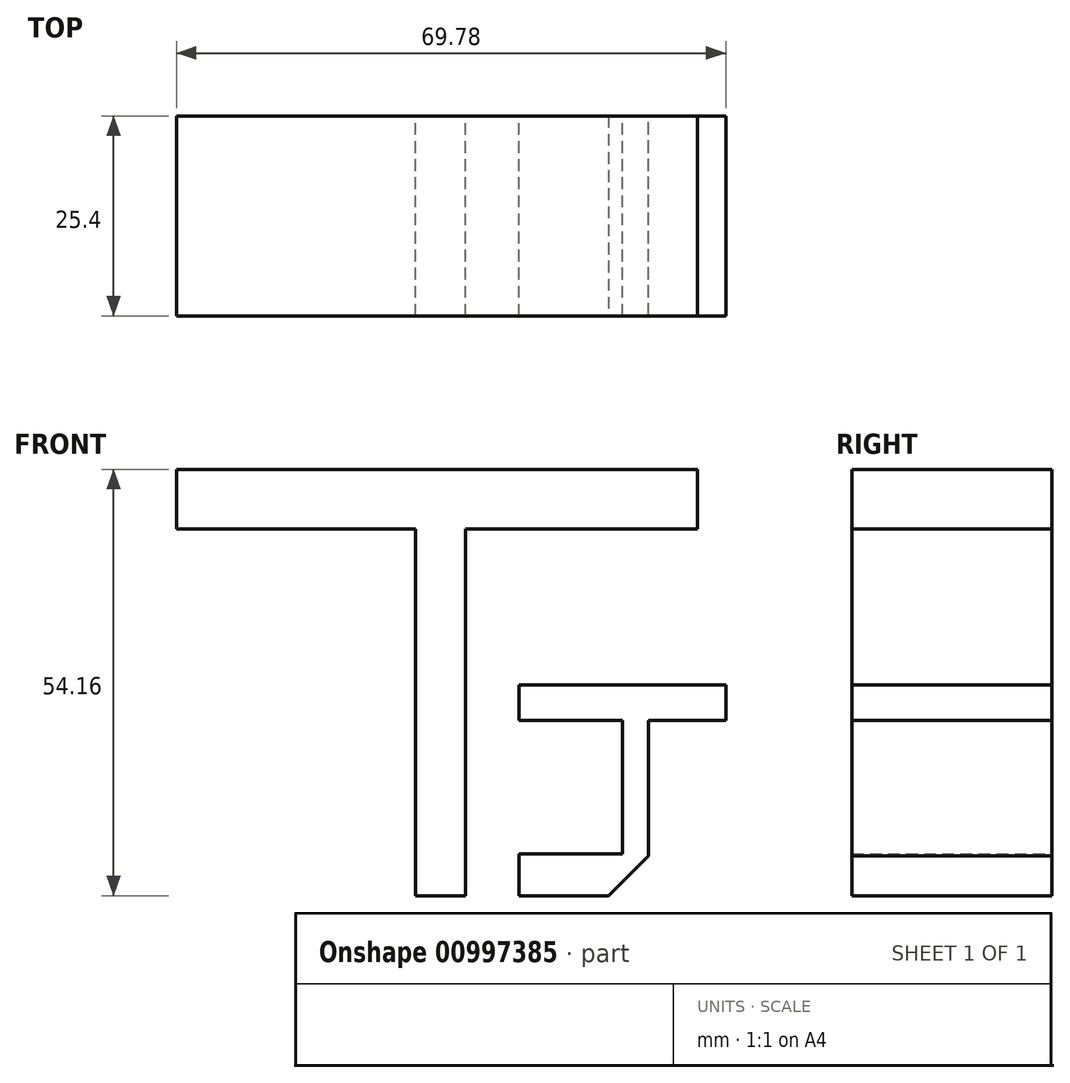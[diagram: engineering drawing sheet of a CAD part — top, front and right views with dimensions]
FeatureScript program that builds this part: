
annotation { "Feature Type Name" : "Feature", "Feature Type Description" : "" }
export const myFeature = defineFeature(function(context is Context, id is Id, definition is map)
    precondition{}
    {
        {
            var Q0;
            Q0=qCreatedBy(makeId("Front.planeOp"),FACE);
            var sketch = newSketch(context, id + "F0", { "sketchPlane" : qUnion([Q0])});
            skLineSegment(sketch, "E0.bottom", {"start": v(-36.7, 54.16) * mm, "end": v(29.44, 54.16) * mm});
            skLineSegment(sketch, "E0.top", {"start": v(-36.7, 46.56) * mm, "end": v(29.44, 46.56) * mm});
            skLineSegment(sketch, "E0.left", {"start": v(-36.7, 54.16) * mm, "end": v(-36.7, 46.56) * mm});
            skLineSegment(sketch, "E0.right", {"start": v(29.44, 54.16) * mm, "end": v(29.44, 46.56) * mm});
            skLineSegment(sketch, "E1.bottom", {"start": v(-6.38, 46.56) * mm, "end": v(0, 46.56) * mm});
            skLineSegment(sketch, "E1.top", {"start": v(-6.38, 0) * mm, "end": v(0, 0) * mm});
            skLineSegment(sketch, "E1.left", {"start": v(-6.38, 46.56) * mm, "end": v(-6.38, 0) * mm});
            skLineSegment(sketch, "E1.right", {"start": v(0, 46.56) * mm, "end": v(0, 0) * mm});
            skSolve(sketch);
        }
        {
            var Q0;
            Q0=makeQuery(id+"F0.imprint","IMPRINT",FACE,{"disambiguationData":[TD([[makeQuery(id+"F0.imprint","IMPRINT",EDGE,{"derivedFrom":sQuery(id+"F0.wireOp",EDGE,"E0.bottom")}),-1.0]])]});
            extrude(context, id + "F1", {"entities" : qUnion([Q0]), "depth" : 25.4 * mm, "offsetDistance" : 25.4 * mm});
        }
        {
            var Q0;
            Q0=makeQuery(id+"F0.imprint","IMPRINT",FACE,{"disambiguationData":[TD([[makeQuery(id+"F0.imprint","IMPRINT",EDGE,{"derivedFrom":sQuery(id+"F0.wireOp",EDGE,"E1.top")}),1.0]])]});
            extrude(context, id + "F2", {"entities" : qUnion([Q0]), "operationType" : NewBodyOperationType.ADD, "depth" : 25.4 * mm, "offsetDistance" : 25.4 * mm});
        }
        {
            var Q0;
            Q0=qCreatedBy(makeId("Front.planeOp"),FACE);
            var sketch = newSketch(context, id + "F3", { "sketchPlane" : qUnion([Q0])});
            skLineSegment(sketch, "E2.bottom", {"start": v(6.81, 26.74) * mm, "end": v(33.07, 26.74) * mm});
            skLineSegment(sketch, "E2.top", {"start": v(6.81, 22.27) * mm, "end": v(33.07, 22.27) * mm});
            skLineSegment(sketch, "E2.left", {"start": v(6.81, 26.74) * mm, "end": v(6.81, 22.27) * mm});
            skLineSegment(sketch, "E2.right", {"start": v(33.07, 26.74) * mm, "end": v(33.07, 22.27) * mm});
            skLineSegment(sketch, "E3.bottom", {"start": v(19.94, 22.27) * mm, "end": v(23.26, 22.27) * mm});
            skLineSegment(sketch, "E3.top", {"start": v(19.94, 0) * mm, "end": v(23.26, 0) * mm});
            skLineSegment(sketch, "E3.left", {"start": v(19.94, 22.27) * mm, "end": v(19.94, 0) * mm});
            skLineSegment(sketch, "E3.right", {"start": v(23.26, 22.27) * mm, "end": v(23.26, 0) * mm});
            skLineSegment(sketch, "E4.bottom", {"start": v(6.81, 0) * mm, "end": v(19.94, 0) * mm});
            skLineSegment(sketch, "E4.top", {"start": v(6.81, 5.32) * mm, "end": v(19.94, 5.32) * mm});
            skLineSegment(sketch, "E4.left", {"start": v(6.81, 0) * mm, "end": v(6.81, 5.32) * mm});
            skLineSegment(sketch, "E4.right", {"start": v(19.94, 0) * mm, "end": v(19.94, 5.32) * mm});
            skSolve(sketch);
        }
        {
            var Q0;
            Q0=makeQuery(id+"F3.imprint","IMPRINT",FACE,{"disambiguationData":[TD([[makeQuery(id+"F3.imprint","IMPRINT",EDGE,{"derivedFrom":sQuery(id+"F3.wireOp",EDGE,"E2.bottom")}),-1.0]])]});
            var Q1;
            {var subQ4=sQuery(id+"F3.wireOp",EDGE,"E3.top");Q1=makeQuery(id+"F3.imprint","IMPRINT",FACE,{"disambiguationData":[TD([[makeQuery(id+"F3.imprint","IMPRINT",EDGE,{"derivedFrom":subQ4}),1.0]])]});}
            var Q2;
            {var subQ0=sQuery(id+"F3.wireOp",EDGE,"E4.bottom");Q2=makeQuery(id+"F3.imprint","IMPRINT",FACE,{"disambiguationData":[TD([[makeQuery(id+"F3.imprint","IMPRINT",EDGE,{"derivedFrom":subQ0}),1.0]])]});}
            extrude(context, id + "F4", {"entities" : qUnion([Q0, Q1, Q2]), "depth" : 25.4 * mm, "offsetDistance" : 25.4 * mm});
        }
        {
            var Q0;
            Q0=makeQuery(id+"F4.opExtrude","SWEPT_EDGE",EDGE,{"disambiguationData":[OSD([sQuery(id+"F3.wireOp",EDGE,"E3.top"),sQuery(id+"F3.wireOp",EDGE,"E3.right")])]});
            chamfer(context, id + "F5", {"entities" : qUnion([Q0]), "width" : 5.08 * mm, "tangentPropagation" : true});
        }
        {
            var Q0;
            {var subQ0=sQuery(id+"F3.wireOp",EDGE,"E3.right");var subQ1=sQuery(id+"F3.wireOp",EDGE,"E3.top");Q0=makeQuery(id+"F5.opChamfer","BLEND_EDGE",EDGE,{"blendedFrom":[makeQuery(id+"F4.opExtrude","SWEPT_EDGE",EDGE,{"disambiguationData":[OSD([subQ1,subQ0])]}),makeQuery(id+"F4.opExtrude","CAP_FACE",FACE,{"disambiguationData":[OSD([sQuery(id+"F3.wireOp",EDGE,"E2.bottom"),sQuery(id+"F3.wireOp",EDGE,"E2.top"),sQuery(id+"F3.wireOp",EDGE,"E2.left"),sQuery(id+"F3.wireOp",EDGE,"E2.right"),subQ1,sQuery(id+"F3.wireOp",EDGE,"E3.left"),subQ0,sQuery(id+"F3.wireOp",EDGE,"E4.bottom"),sQuery(id+"F3.wireOp",EDGE,"E4.top"),sQuery(id+"F3.wireOp",EDGE,"E4.left")])],"isStart":false})],"blendedInto":[makeQuery(id+"F4.opExtrude","CAP_FACE",FACE,{"disambiguationData":[OSD([sQuery(id+"F3.wireOp",EDGE,"E2.bottom"),sQuery(id+"F3.wireOp",EDGE,"E2.top"),sQuery(id+"F3.wireOp",EDGE,"E2.left"),sQuery(id+"F3.wireOp",EDGE,"E2.right"),subQ1,sQuery(id+"F3.wireOp",EDGE,"E3.left"),subQ0,sQuery(id+"F3.wireOp",EDGE,"E4.bottom"),sQuery(id+"F3.wireOp",EDGE,"E4.top"),sQuery(id+"F3.wireOp",EDGE,"E4.left")])],"isStart":false})]});}
            fillet(context, id + "F6", {"entities" : qUnion([Q0]), "radius" : 0.1 * mm, "tangentPropagation" : true, "allowEdgeOverflow" : false});
        }
    });
